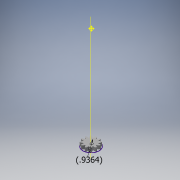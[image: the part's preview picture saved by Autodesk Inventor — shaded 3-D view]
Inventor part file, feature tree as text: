
AUTODESK INVENTOR PART (.ipt)
format: ipt  version: 2017 (Build 210142000, 142)  size: 450,560 bytes
history: native  units: mm
features: other x24, loft x2, pattern_circular x2, sketch x2
ambient origin geometry x6: Origin, XZ Plane, X Axis, Y Axis, Z Axis, Center Point
bodies: Solid1 (feature_tree)
feature tree (30):
  other  "Top Point"
  other  "Mesh Plane2"
  other  "Teeth Body"
  other  "Start Point"
  other  "Tooth Plane"
  other  "Start Sketch"
  other  "End Point"
  other  "3D Sketch Right"
  other  "End Plane Right"
  loft  "Loft Right"
  pattern_circular  "Circular Pattern Right"  [2 undecoded]
  other  "3D Sketch Left"
  other  "End Plane Left"
  loft  "Loft Left"
  pattern_circular  "Circular Pattern Left"  Angle=90.0deg  [1 undecoded]
  other  "Fix Body"
  sketch  "Sketch8"  dims[d2=23.785175mm d3=5.08mm d4=148.895202mm d5=90.0deg d7=5.001282mm d8=5.466242mm d9=7.460675mm d11=5.257847mm d12=4.830224mm d15=5.279282mm d16=7.2055mm d17=0.0mm d18=90.0deg d19=0.0mm d20=90.0deg d21=120.0mm d22=360.0deg d26=126.354885mm d27=5.245668mm d28=20.32mm d29=-0.680765mm d30=4.830224mm d31=5.279282mm d32=7.2055mm d35=0.0mm d37=0.0mm d39=0.0mm d40=90.0deg d41=120.0mm d42=360.0deg d46=90.0deg d47=90.0deg d48=0.0mm d49=0.0mm d50=90.0deg d51=15.0deg d52=0.0mm d53=0.0mm d54=0.0mm d56=11.461497mm d57=12.987282mm d58=7.936422mm d59=12.543082mm d60=7.664975mm d61=12.543082mm d62=7.664975mm d63=90.0deg d64=90.0deg d65=126.354885mm d66=31.5mm d67=20.32mm d68=-0.680765mm d69=5.245668mm d70=5.279282mm d71=7.2055mm d72=4.830224mm d73=7.664975mm d74=12.543082mm d75=0.0mm d76=90.0deg d77=0.0mm d78=90.0deg d79=0.0mm d80=90.0deg d81=120.0mm d82=360.0deg d84=10.0mm d85=20.0mm d86=20.0mm d87=10.0mm d88=0.0mm d89=0.0mm]
  other  "Mesh Plane"
  other  "Top Plane"
  other  "Teeth Body Sketch"
  other  "End Plane"
  other  "End Sketch"
  other  "Helical Curve Left"
  other  "End Sketch Left"
  other  "Body Sketch"
  sketch  "Sketch6"  dims[d0=20.32mm d1=16.687766mm]
  other  "Srf1"
  other  "Helical Curve Right"
  other  "End Sketch Right"
  other  "Pitch Diameter"
note: 3 required parameter values undecoded (feature->parameter linkage not recoverable at this tier; creation-order binding heuristic only, values carry confidence <= 0.55)
